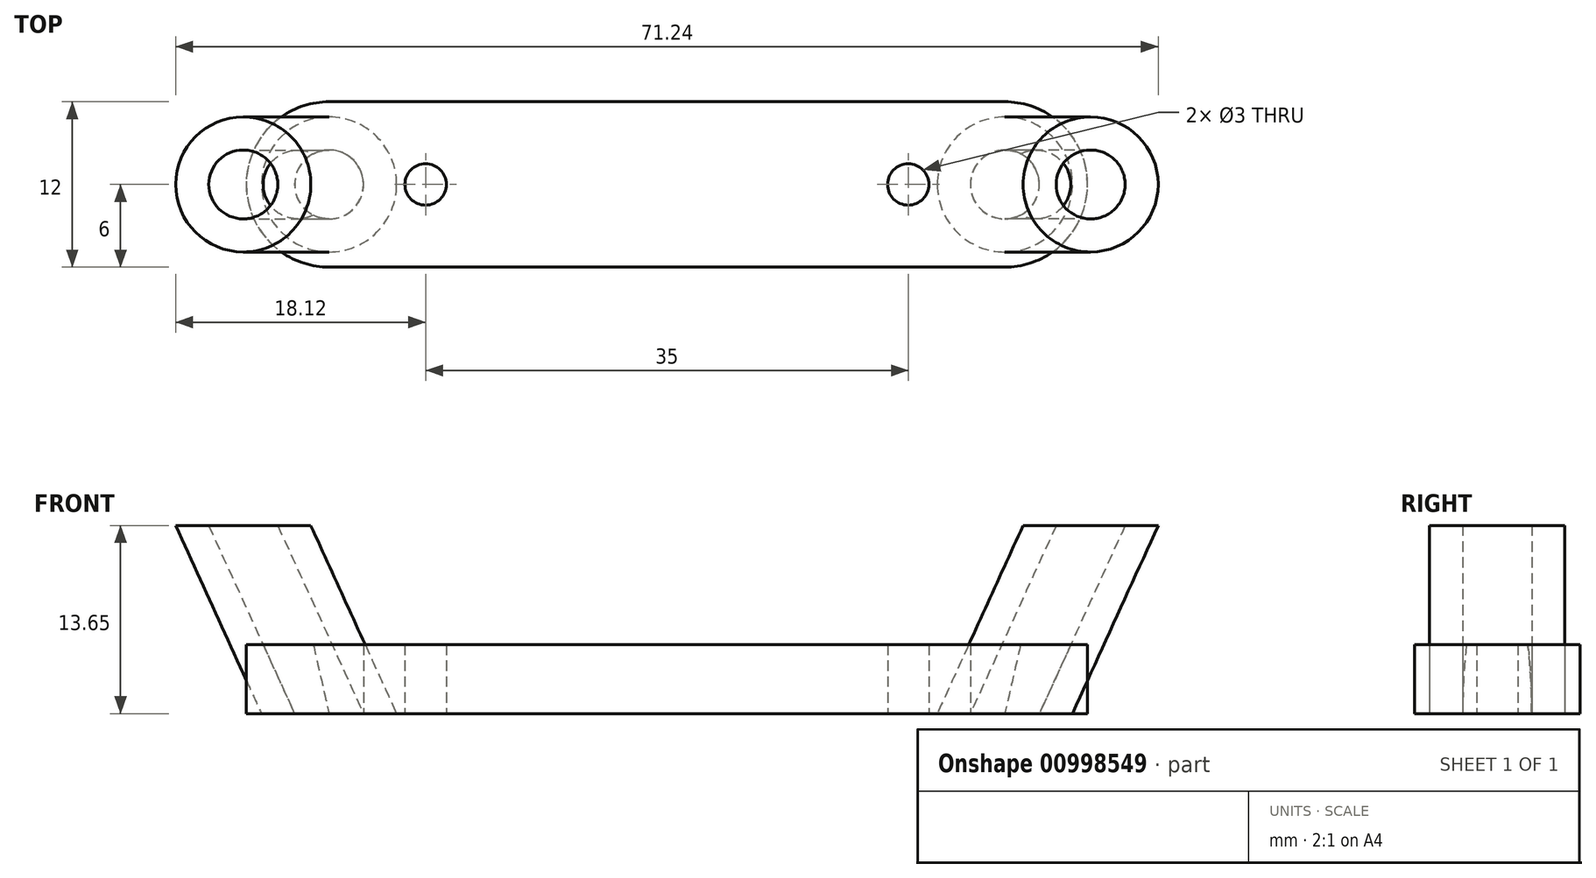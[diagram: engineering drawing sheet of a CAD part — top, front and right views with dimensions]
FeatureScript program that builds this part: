
annotation { "Feature Type Name" : "Feature", "Feature Type Description" : "" }
export const myFeature = defineFeature(function(context is Context, id is Id, definition is map)
    precondition{}
    {
        {
            var Q0;
            Q0=qCreatedBy(makeId("Top.planeOp"),FACE);
            var sketch = newSketch(context, id + "F0", { "sketchPlane" : qUnion([Q0])});
            skLineSegment(sketch, "E0.bottom", {"start": v(-24.5, 6) * mm, "end": v(24.5, 6) * mm});
            skLineSegment(sketch, "E0.top", {"start": v(-24.5, -6) * mm, "end": v(24.5, -6) * mm});
            skLineSegment(sketch, "E0.left", {"start": v(-24.5, 6) * mm, "end": v(-24.5, -6) * mm});
            skLineSegment(sketch, "E0.right", {"start": v(24.5, 6) * mm, "end": v(24.5, -6) * mm});
            skPoint(sketch, "E0.middle", {"position": v(0, 0) * mm});
            skCircle(sketch, "E1", {"center": v(-24.5, 0) * mm, "radius": 4.9 * mm});
            skCircle(sketch, "E2", {"center": v(24.5, 0) * mm, "radius": 4.9 * mm});
            skCircle(sketch, "E3", {"center": v(17.5, 0) * mm, "radius": 1.5 * mm});
            skCircle(sketch, "E4", {"center": v(-17.5, 0) * mm, "radius": 1.5 * mm});
            skLineSegment(sketch, "E5", {"start": v(0, 0) * mm, "end": v(-17.5, 0) * mm, "construction": true});
            skLineSegment(sketch, "E6", {"start": v(-17.5, 0) * mm, "end": v(-24.5, 0) * mm, "construction": true});
            skLineSegment(sketch, "E7", {"start": v(0, 0) * mm, "end": v(17.5, 0) * mm, "construction": true});
            skLineSegment(sketch, "E8", {"start": v(17.5, 0) * mm, "end": v(24.5, 0) * mm, "construction": true});
            skLineSegment(sketch, "E9", {"start": v(-17.5, 0) * mm, "end": v(17.5, 0) * mm, "construction": true});
            skCircle(sketch, "E10.0", {"center": v(-24.5, 0) * mm, "radius": 2.5 * mm});
            skCircle(sketch, "E11", {"center": v(-24.5, 0) * mm, "radius": 6 * mm});
            skCircle(sketch, "E12", {"center": v(24.5, 0) * mm, "radius": 6 * mm});
            skCircle(sketch, "E13.MirrorC", {"center": v(24.5, 0) * mm, "radius": 2.5 * mm});
            skLineSegment(sketch, "E14", {"start": v(0, 6) * mm, "end": v(0, -6) * mm, "construction": true});
            skSolve(sketch);
        }
        {
            var Q0;
            Q0=qCreatedBy(makeId("Front.planeOp"),FACE);
            var sketch = newSketch(context, id + "F1", { "sketchPlane" : qUnion([Q0])});
            skLineSegment(sketch, "E15", {"start": v(-24.5, 0) * mm, "end": v(-30.72, 13.65) * mm});
            skLineSegment(sketch, "E16.MirrorCS", {"start": v(24.5, 0) * mm, "end": v(30.72, 13.65) * mm});
            skSolve(sketch);
        }
        {
            var Q0;
            {var subQ2=sQuery(id+"F0.wireOp",EDGE,"E0.bottom");Q0=makeQuery(id+"F0.imprint","IMPRINT",FACE,{"disambiguationData":[TD([[makeQuery(id+"F0.imprint","IMPRINT",EDGE,{"derivedFrom":subQ2}),-1.0]])]});}
            var Q1;
            {var subQ1=sQuery(id+"F0.wireOp",EDGE,"E0.left");var subQ3=sQuery(id+"F0.wireOp",EDGE,"E10.0");var subQ4=makeQuery(id+"F0.imprint","INTERSECT",VERTEX,{"disambiguationData":[OD(0.0)],"derivedFrom":[subQ1,subQ3]});Q1=makeQuery(id+"F0.imprint","IMPRINT",FACE,{"disambiguationData":[TD([[makeQuery(id+"F0.imprint","IMPRINT",EDGE,{"disambiguationData":[TD([[subQ4,1.0]])],"derivedFrom":subQ3}),-1.0]])]});}
            var Q2;
            {var subQ1=sQuery(id+"F0.wireOp",EDGE,"E0.right");var subQ3=sQuery(id+"F0.wireOp",EDGE,"E13.MirrorC");var subQ4=makeQuery(id+"F0.imprint","INTERSECT",VERTEX,{"disambiguationData":[OD(0.0)],"derivedFrom":[subQ1,subQ3]});Q2=makeQuery(id+"F0.imprint","IMPRINT",FACE,{"disambiguationData":[TD([[makeQuery(id+"F0.imprint","IMPRINT",EDGE,{"disambiguationData":[TD([[subQ4,-1.0]])],"derivedFrom":subQ3}),-1.0]])]});}
            var Q3;
            {var subQ1=sQuery(id+"F0.wireOp",EDGE,"E0.right");var subQ3=sQuery(id+"F0.wireOp",EDGE,"E2");var subQ4=makeQuery(id+"F0.imprint","INTERSECT",VERTEX,{"disambiguationData":[OD(0.0)],"derivedFrom":[subQ1,subQ3]});Q3=makeQuery(id+"F0.imprint","IMPRINT",FACE,{"disambiguationData":[TD([[makeQuery(id+"F0.imprint","IMPRINT",EDGE,{"disambiguationData":[TD([[subQ4,1.0]])],"derivedFrom":subQ3}),-1.0]])]});}
            var Q4;
            {var subQ0=sQuery(id+"F0.wireOp",EDGE,"E2");var subQ1=sQuery(id+"F0.wireOp",EDGE,"E0.right");var subQ2=makeQuery(id+"F0.imprint","INTERSECT",VERTEX,{"disambiguationData":[OD(0.0)],"derivedFrom":[subQ1,subQ0]});Q4=makeQuery(id+"F0.imprint","IMPRINT",FACE,{"disambiguationData":[TD([[makeQuery(id+"F0.imprint","IMPRINT",EDGE,{"disambiguationData":[TD([[subQ2,-1.0]])],"derivedFrom":subQ0}),-1.0]])]});}
            var Q5;
            {var subQ4=sQuery(id+"F0.wireOp",EDGE,"E1");var subQ5=sQuery(id+"F0.wireOp",EDGE,"E0.left");var subQ6=makeQuery(id+"F0.imprint","INTERSECT",VERTEX,{"disambiguationData":[OD(0.0)],"derivedFrom":[subQ5,subQ4]});Q5=makeQuery(id+"F0.imprint","IMPRINT",FACE,{"disambiguationData":[TD([[makeQuery(id+"F0.imprint","IMPRINT",EDGE,{"disambiguationData":[TD([[subQ6,1.0]])],"derivedFrom":subQ4}),-1.0]])]});}
            var Q6;
            {var subQ1=sQuery(id+"F0.wireOp",EDGE,"E0.left");var subQ3=sQuery(id+"F0.wireOp",EDGE,"E1");var subQ4=makeQuery(id+"F0.imprint","INTERSECT",VERTEX,{"disambiguationData":[OD(0.0)],"derivedFrom":[subQ1,subQ3]});Q6=makeQuery(id+"F0.imprint","IMPRINT",FACE,{"disambiguationData":[TD([[makeQuery(id+"F0.imprint","IMPRINT",EDGE,{"disambiguationData":[TD([[subQ4,-1.0]])],"derivedFrom":subQ3}),-1.0]])]});}
            var Q7;
            {var subQ0=sQuery(id+"F0.wireOp",EDGE,"E2");var subQ1=sQuery(id+"F0.wireOp",EDGE,"E0.right");var subQ2=makeQuery(id+"F0.imprint","INTERSECT",VERTEX,{"disambiguationData":[OD(0.0)],"derivedFrom":[subQ1,subQ0]});Q7=makeQuery(id+"F0.imprint","IMPRINT",FACE,{"disambiguationData":[TD([[makeQuery(id+"F0.imprint","IMPRINT",EDGE,{"disambiguationData":[TD([[subQ2,-1.0]])],"derivedFrom":subQ1}),1.0]])]});}
            var Q8;
            {var subQ0=sQuery(id+"F0.wireOp",EDGE,"E1");var subQ1=sQuery(id+"F0.wireOp",EDGE,"E0.left");var subQ2=makeQuery(id+"F0.imprint","INTERSECT",VERTEX,{"disambiguationData":[OD(0.0)],"derivedFrom":[subQ1,subQ0]});Q8=makeQuery(id+"F0.imprint","IMPRINT",FACE,{"disambiguationData":[TD([[makeQuery(id+"F0.imprint","IMPRINT",EDGE,{"disambiguationData":[TD([[subQ2,-1.0]])],"derivedFrom":subQ1}),-1.0]])]});}
            extrude(context, id + "F2", {"entities" : qUnion([Q0, Q1, Q2, Q3, Q4, Q5, Q6, Q7, Q8]), "depth" : 5 * mm, "offsetDistance" : 25 * mm});
        }
        {
            var Q0;
            {var subQ0=sQuery(id+"F0.wireOp",EDGE,"E10.0");var subQ1=sQuery(id+"F0.wireOp",EDGE,"E0.left");var subQ2=makeQuery(id+"F0.imprint","INTERSECT",VERTEX,{"disambiguationData":[OD(0.0)],"derivedFrom":[subQ1,subQ0]});Q0=makeQuery(id+"F0.imprint","IMPRINT",FACE,{"disambiguationData":[TD([[makeQuery(id+"F0.imprint","IMPRINT",EDGE,{"disambiguationData":[TD([[subQ2,-1.0]])],"derivedFrom":subQ1}),1.0]])]});}
            var Q1;
            {var subQ0=sQuery(id+"F0.wireOp",EDGE,"E10.0");var subQ1=sQuery(id+"F0.wireOp",EDGE,"E0.left");var subQ2=makeQuery(id+"F0.imprint","INTERSECT",VERTEX,{"disambiguationData":[OD(0.0)],"derivedFrom":[subQ1,subQ0]});Q1=makeQuery(id+"F0.imprint","IMPRINT",FACE,{"disambiguationData":[TD([[makeQuery(id+"F0.imprint","IMPRINT",EDGE,{"disambiguationData":[TD([[subQ2,-1.0]])],"derivedFrom":subQ1}),-1.0]])]});}
            var Q2;
            {var subQ0=sQuery(id+"F0.wireOp",EDGE,"E1");var subQ1=sQuery(id+"F0.wireOp",EDGE,"E0.left");var subQ2=makeQuery(id+"F0.imprint","INTERSECT",VERTEX,{"disambiguationData":[OD(0.0)],"derivedFrom":[subQ1,subQ0]});Q2=makeQuery(id+"F0.imprint","IMPRINT",FACE,{"disambiguationData":[TD([[makeQuery(id+"F0.imprint","IMPRINT",EDGE,{"disambiguationData":[TD([[subQ2,-1.0]])],"derivedFrom":subQ1}),1.0]])]});}
            var Q3;
            {var subQ0=sQuery(id+"F0.wireOp",EDGE,"E1");var subQ1=sQuery(id+"F0.wireOp",EDGE,"E0.left");var subQ2=makeQuery(id+"F0.imprint","INTERSECT",VERTEX,{"disambiguationData":[OD(0.0)],"derivedFrom":[subQ1,subQ0]});Q3=makeQuery(id+"F0.imprint","IMPRINT",FACE,{"disambiguationData":[TD([[makeQuery(id+"F0.imprint","IMPRINT",EDGE,{"disambiguationData":[TD([[subQ2,-1.0]])],"derivedFrom":subQ1}),-1.0]])]});}
            var Q4;
            Q4=sQuery(id+"FmFBqTdY2TZA42R_1.wireOp",EDGE,"54cd2d33-c72a-4899-93a6-d76ce68880c00.MirrorC");
            var Q5;
            Q5=sQuery(id+"FmFBqTdY2TZA42R_1.wireOp",EDGE,"0932ff46-98bd-4906-b015-36eb4d5494440.MirrorC");
            var Q6;
            Q6=sQuery(id+"F1.wireOp",EDGE,"E15");
            sweep(context, id + "F3", {"profiles" : qUnion([Q0, Q1, Q2, Q3]), "surfaceOperationType" : NewSurfaceOperationType.ADD, "surfaceProfiles" : qUnion([Q4, Q5]), "path" : qUnion([Q6])});
        }
        {
            var Q0;
            Q0=makeQuery(id+"F3.opSweep","SWEPT_BODY",BODY,{"disambiguationData":[OSD([sQuery(id+"F0.wireOp",EDGE,"E1"),sQuery(id+"F1.wireOp",EDGE,"E15")])]});
            var Q1;
            Q1=qCreatedBy(makeId("Right.planeOp"),FACE);
            mirror(context, id + "F4", {"entities" : qUnion([Q0]), "mirrorPlane" : qUnion([Q1])});
        }
        {
            var Q0;
            {var subQ0=sQuery(id+"F0.wireOp",EDGE,"E10.0");var subQ1=sQuery(id+"F0.wireOp",EDGE,"E0.left");var subQ2=makeQuery(id+"F0.imprint","INTERSECT",VERTEX,{"disambiguationData":[OD(0.0)],"derivedFrom":[subQ1,subQ0]});Q0=makeQuery(id+"F0.imprint","IMPRINT",FACE,{"disambiguationData":[TD([[makeQuery(id+"F0.imprint","IMPRINT",EDGE,{"disambiguationData":[TD([[subQ2,-1.0]])],"derivedFrom":subQ1}),1.0]])]});}
            var Q1;
            {var subQ0=sQuery(id+"F0.wireOp",EDGE,"E10.0");var subQ1=sQuery(id+"F0.wireOp",EDGE,"E0.left");var subQ2=makeQuery(id+"F0.imprint","INTERSECT",VERTEX,{"disambiguationData":[OD(0.0)],"derivedFrom":[subQ1,subQ0]});Q1=makeQuery(id+"F0.imprint","IMPRINT",FACE,{"disambiguationData":[TD([[makeQuery(id+"F0.imprint","IMPRINT",EDGE,{"disambiguationData":[TD([[subQ2,-1.0]])],"derivedFrom":subQ1}),-1.0]])]});}
            var Q2;
            Q2=sQuery(id+"F0.wireOp",EDGE,"E13.MirrorC");
            var Q3;
            Q3=sQuery(id+"F1.wireOp",EDGE,"E15");
            sweep(context, id + "F5", {"operationType" : NewBodyOperationType.REMOVE, "profiles" : qUnion([Q0, Q1]), "surfaceProfiles" : qUnion([Q2]), "path" : qUnion([Q3])});
        }
        {
            var Q0;
            {var subQ0=sQuery(id+"F0.wireOp",EDGE,"E13.MirrorC");var subQ1=sQuery(id+"F0.wireOp",EDGE,"E0.right");var subQ2=makeQuery(id+"F0.imprint","INTERSECT",VERTEX,{"disambiguationData":[OD(0.0)],"derivedFrom":[subQ1,subQ0]});Q0=makeQuery(id+"F0.imprint","IMPRINT",FACE,{"disambiguationData":[TD([[makeQuery(id+"F0.imprint","IMPRINT",EDGE,{"disambiguationData":[TD([[subQ2,-1.0]])],"derivedFrom":subQ1}),1.0]])]});}
            var Q1;
            {var subQ0=sQuery(id+"F0.wireOp",EDGE,"E13.MirrorC");var subQ1=sQuery(id+"F0.wireOp",EDGE,"E0.right");var subQ2=makeQuery(id+"F0.imprint","INTERSECT",VERTEX,{"disambiguationData":[OD(0.0)],"derivedFrom":[subQ1,subQ0]});Q1=makeQuery(id+"F0.imprint","IMPRINT",FACE,{"disambiguationData":[TD([[makeQuery(id+"F0.imprint","IMPRINT",EDGE,{"disambiguationData":[TD([[subQ2,-1.0]])],"derivedFrom":subQ1}),-1.0]])]});}
            var Q2;
            Q2=sQuery(id+"F0.wireOp",EDGE,"E13.MirrorC");
            var Q3;
            Q3=sQuery(id+"F1.wireOp",EDGE,"E16.MirrorCS");
            var Q4;
            Q4=sQuery(id+"F1.wireOp",EDGE,"E16.MirrorCS");
            sweep(context, id + "F6", {"operationType" : NewBodyOperationType.REMOVE, "profiles" : qUnion([Q0, Q1]), "surfaceProfiles" : qUnion([Q2, Q3]), "path" : qUnion([Q4])});
        }
    });
